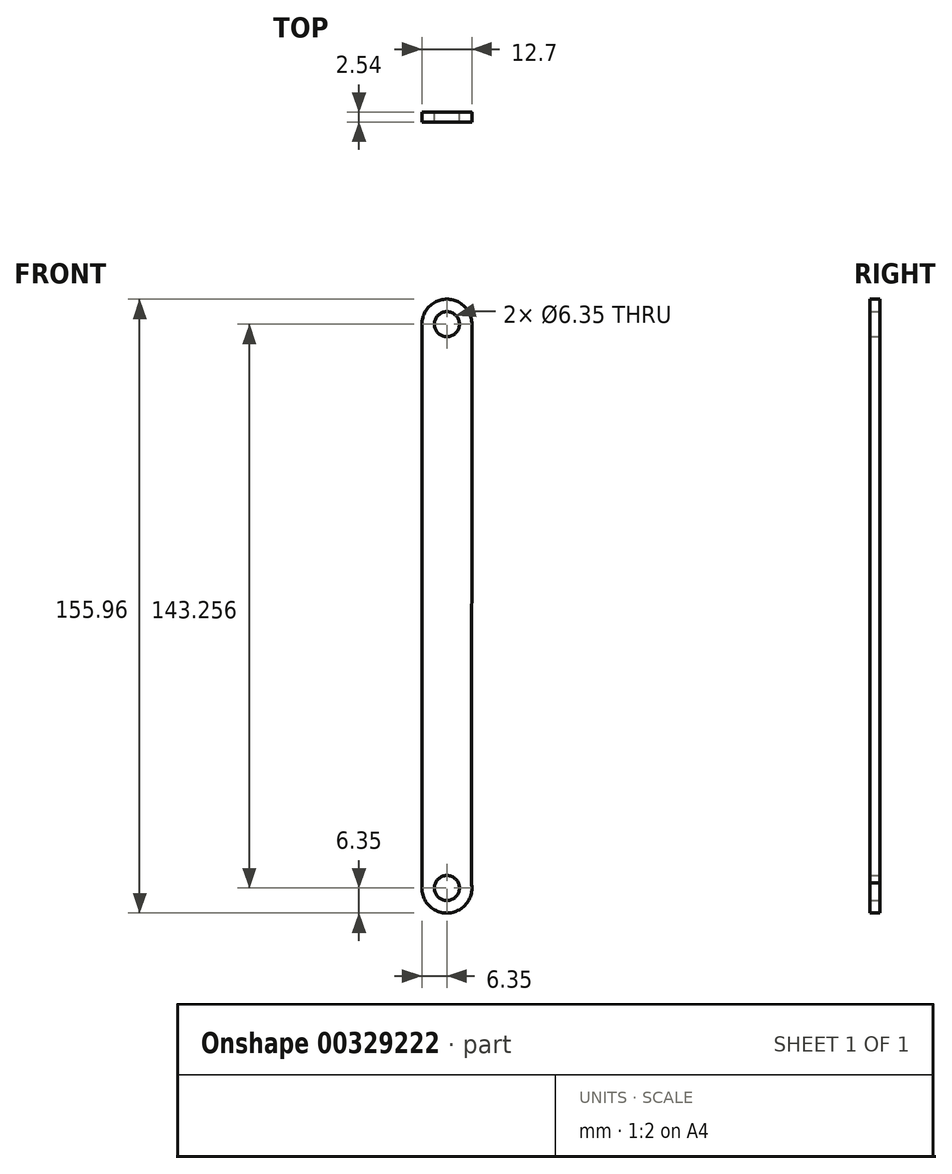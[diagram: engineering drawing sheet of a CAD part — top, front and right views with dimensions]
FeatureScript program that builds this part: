
annotation { "Feature Type Name" : "Feature", "Feature Type Description" : "" }
export const myFeature = defineFeature(function(context is Context, id is Id, definition is map)
    precondition{}
    {
        {
            var Q0;
            Q0=qCreatedBy(makeId("Front.planeOp"),FACE);
            var sketch = newSketch(context, id + "F0", { "sketchPlane" : qUnion([Q0])});
            skCircle(sketch, "E0", {"center": v(0, 0) * mm, "radius": 3.18 * mm});
            skCircle(sketch, "E1", {"center": v(0, 143.26) * mm, "radius": 6.35 * mm});
            skCircle(sketch, "E2", {"center": v(0, 143.26) * mm, "radius": 3.18 * mm});
            skCircle(sketch, "E3", {"center": v(0, 0) * mm, "radius": 6.35 * mm});
            skLineSegment(sketch, "E4", {"start": v(-6.35, 143.26) * mm, "end": v(-6.35, 0) * mm});
            skLineSegment(sketch, "E5", {"start": v(6.35, 143.25) * mm, "end": v(6.22, 1.3) * mm});
            skSolve(sketch);
        }
        {
            var Q0;
            Q0=makeQuery(id+"F0.imprint","IMPRINT",FACE,{"disambiguationData":[TD([[makeQuery(id+"F0.imprint","IMPRINT",EDGE,{"derivedFrom":sQuery(id+"F0.wireOp",EDGE,"E0")}),-1.0]])]});
            var Q1;
            {var subQ0=sQuery(id+"F0.wireOp",EDGE,"E4");Q1=makeQuery(id+"F0.imprint","IMPRINT",FACE,{"disambiguationData":[TD([[makeQuery(id+"F0.imprint","IMPRINT",EDGE,{"derivedFrom":subQ0}),1.0]])]});}
            var Q2;
            Q2=makeQuery(id+"F0.imprint","IMPRINT",FACE,{"disambiguationData":[TD([[makeQuery(id+"F0.imprint","IMPRINT",EDGE,{"derivedFrom":sQuery(id+"F0.wireOp",EDGE,"E2")}),-1.0]])]});
            extrude(context, id + "F1", {"entities" : qUnion([Q0, Q1, Q2]), "depth" : 2.54 * mm});
        }
    });
